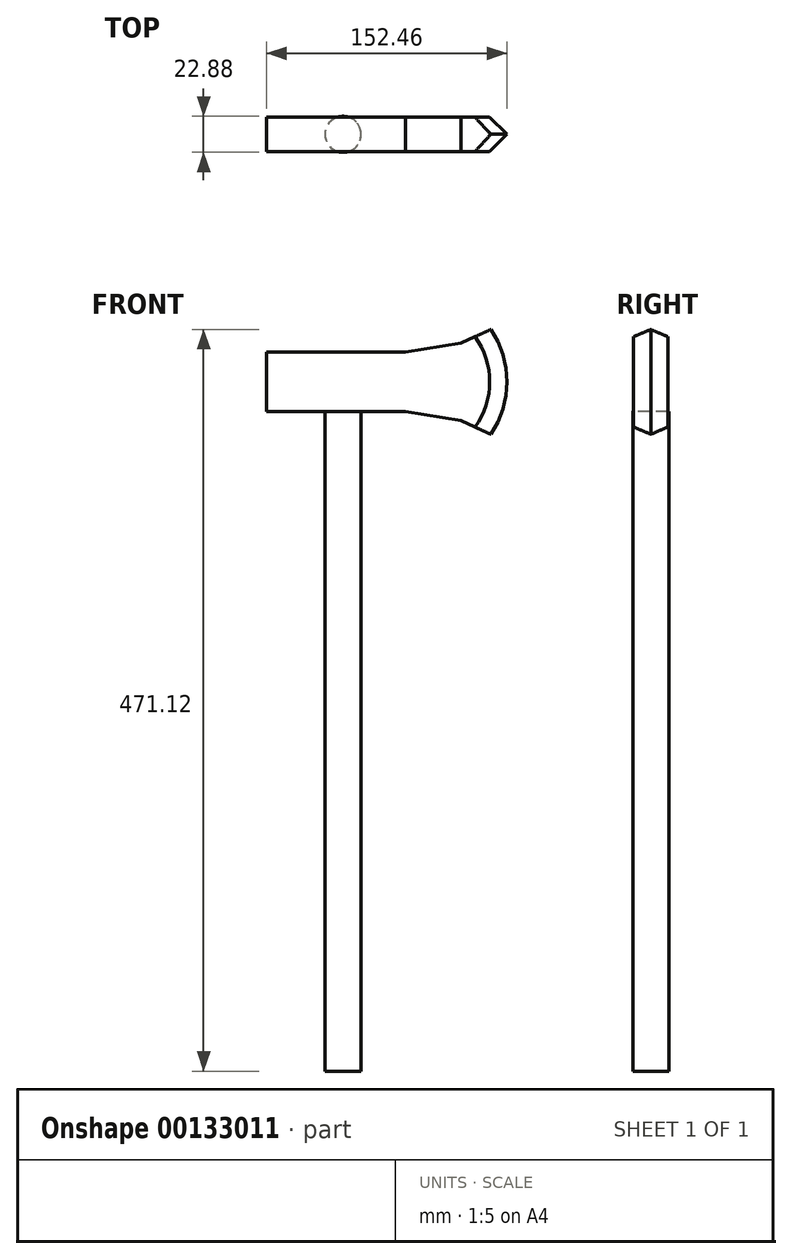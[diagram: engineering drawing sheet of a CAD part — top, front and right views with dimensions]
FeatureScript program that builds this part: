
annotation { "Feature Type Name" : "Feature", "Feature Type Description" : "" }
export const myFeature = defineFeature(function(context is Context, id is Id, definition is map)
    precondition{}
    {
        {
            var Q0;
            Q0=qCreatedBy(makeId("Top.planeOp"),FACE);
            var sketch = newSketch(context, id + "F0", { "sketchPlane" : qUnion([Q0])});
            skCircle(sketch, "E0", {"center": v(0, 0) * mm, "radius": 11.44 * mm});
            skSolve(sketch);
        }
        {
            var Q0;
            Q0 = qSketchRegion(id + "F0", true);
            extrude(context, id + "F1", {"entities" : qUnion([Q0]), "depth" : 419.02 * mm});
        }
        {
            var Q0;
            Q0=qCreatedBy(makeId("Front.planeOp"),FACE);
            var sketch = newSketch(context, id + "F2", { "sketchPlane" : qUnion([Q0])});
            skLineSegment(sketch, "E1", {"start": v(-48.47, 418.97) * mm, "end": v(39.71, 418.97) * mm});
            skLineSegment(sketch, "E2", {"start": v(-48.47, 418.97) * mm, "end": v(-48.47, 456.7) * mm});
            skLineSegment(sketch, "E3", {"start": v(-48.47, 456.7) * mm, "end": v(39.71, 456.7) * mm});
            skLineSegment(sketch, "E4", {"start": v(39.71, 456.7) * mm, "end": v(74.81, 462.4) * mm});
            skLineSegment(sketch, "E5", {"start": v(74.81, 462.4) * mm, "end": v(95.6, 471.9) * mm});
            skLineSegment(sketch, "E6", {"start": v(39.71, 418.97) * mm, "end": v(74.81, 413.27) * mm});
            skLineSegment(sketch, "E7", {"start": v(74.81, 413.27) * mm, "end": v(95.6, 403.78) * mm});
            skArc(sketch, "E8", {"start": v(95.6, 403.78) * mm, "mid": v(105.85, 437.84) * mm, "end": v(95.6, 471.9) * mm});
            skSolve(sketch);
        }
        {
            var Q0;
            Q0=makeQuery(id+"F2.imprint","IMPRINT",FACE,{"disambiguationData":[TD([[makeQuery(id+"F2.imprint","IMPRINT",EDGE,{"derivedFrom":sQuery(id+"F2.wireOp",EDGE,"E1")}),1.0]])]});
            extrude(context, id + "F3", {"entities" : qUnion([Q0]), "operationType" : NewBodyOperationType.ADD, "depth" : 10.85 * mm, "hasSecondDirection" : true, "secondDirectionOppositeDirection" : true, "secondDirectionDepth" : 10.85 * mm});
        }
        {
            var Q0;
            Q0=makeQuery(id+"F3.opExtrude","CAP_EDGE",EDGE,{"disambiguationData":[OSD([sQuery(id+"F2.wireOp",EDGE,"E8")])],"isStart":false});
            var Q1;
            Q1=makeQuery(id+"F3.opExtrude","CAP_EDGE",EDGE,{"disambiguationData":[OSD([sQuery(id+"F2.wireOp",EDGE,"E8")])],"isStart":true});
            chamfer(context, id + "F4", {"entities" : qUnion([Q0, Q1]), "width" : 12.7 * mm, "tangentPropagation" : true});
        }
    });
